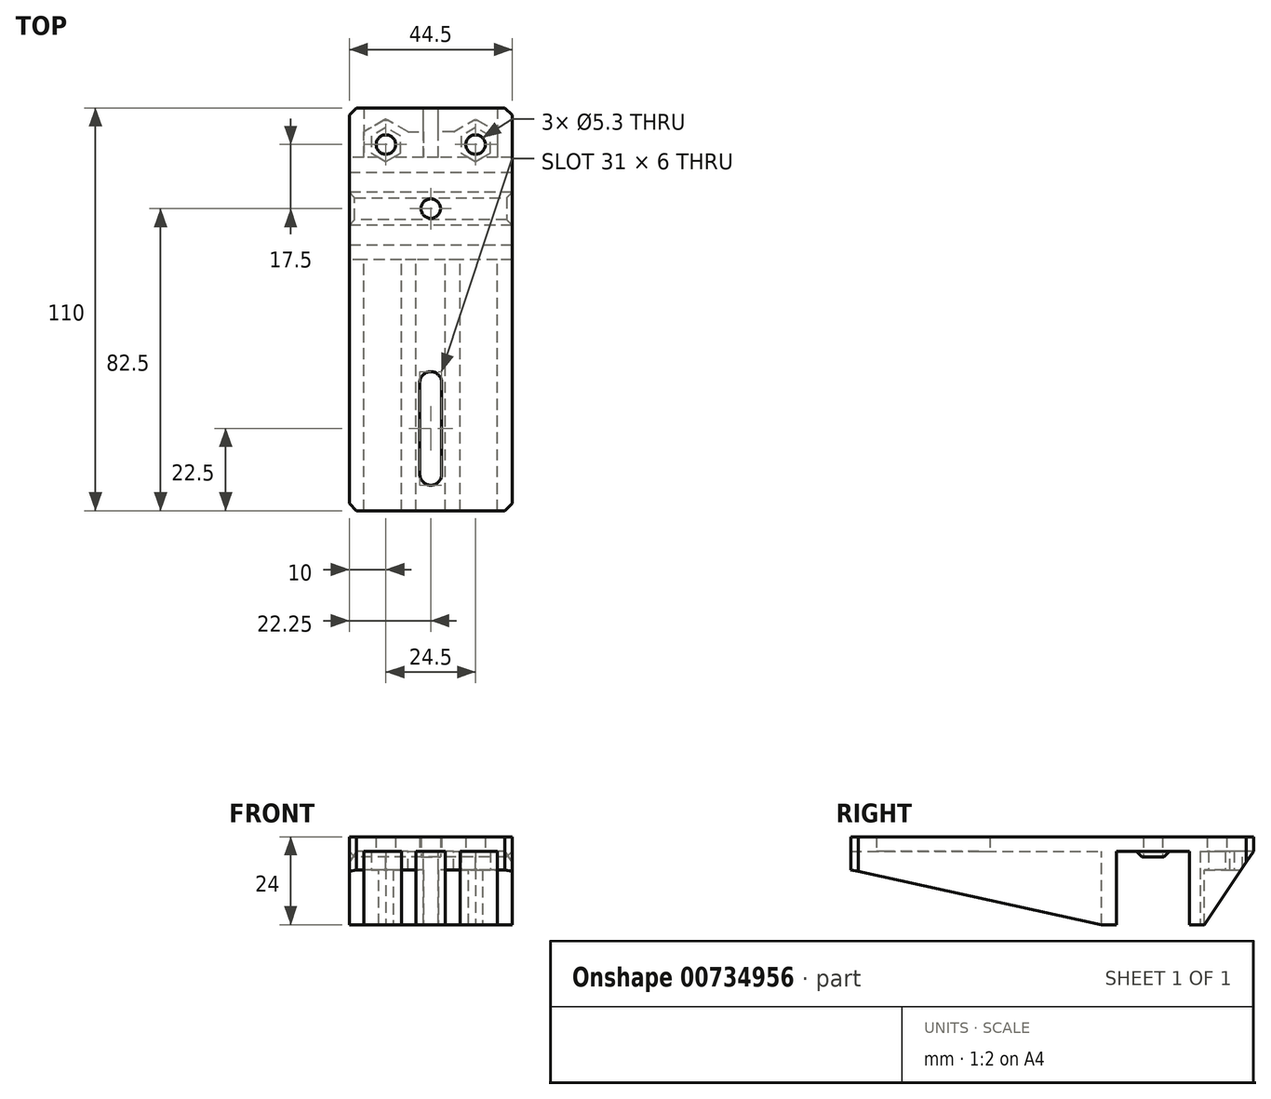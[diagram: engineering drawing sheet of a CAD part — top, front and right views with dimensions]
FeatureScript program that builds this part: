
annotation { "Feature Type Name" : "Feature", "Feature Type Description" : "" }
export const myFeature = defineFeature(function(context is Context, id is Id, definition is map)
    precondition{}
    {
        {
            var Q0;
            Q0=qCreatedBy(makeId("Top.planeOp"),FACE);
            var sketch = newSketch(context, id + "F0", { "sketchPlane" : qUnion([Q0])});
            skLineSegment(sketch, "E0.bottom", {"start": v(0, 0) * mm, "end": v(44.5, 0) * mm});
            skLineSegment(sketch, "E0.top", {"start": v(0, 110) * mm, "end": v(44.5, 110) * mm});
            skLineSegment(sketch, "E0.left", {"start": v(0, 0) * mm, "end": v(0, 110) * mm});
            skLineSegment(sketch, "E0.right", {"start": v(44.5, 0) * mm, "end": v(44.5, 110) * mm});
            skCircle(sketch, "E1", {"center": v(22.25, 10) * mm, "radius": 6.12 * mm, "construction": true});
            skPoint(sketch, "E1.centerSnap0", {"position": v(22.25, 0) * mm});
            skCircle(sketch, "E2", {"center": v(10, 100) * mm, "radius": 6.12 * mm, "construction": true});
            skCircle(sketch, "E3", {"center": v(34.5, 100) * mm, "radius": 6.12 * mm, "construction": true});
            skLineSegment(sketch, "E4", {"start": v(16.12, 100) * mm, "end": v(16.13, 10) * mm, "construction": true});
            skLineSegment(sketch, "E5", {"start": v(28.37, 10) * mm, "end": v(28.37, 100) * mm, "construction": true});
            skCircle(sketch, "E6", {"center": v(10, 100) * mm, "radius": 2.65 * mm});
            skCircle(sketch, "E7", {"center": v(34.5, 100) * mm, "radius": 2.65 * mm});
            skLineSegment(sketch, "E8", {"start": v(25.25, 10) * mm, "end": v(25.25, 35) * mm});
            skLineSegment(sketch, "E9", {"start": v(19.25, 35) * mm, "end": v(19.25, 10) * mm});
            skArc(sketch, "E10", {"start": v(19.25, 35) * mm, "mid": v(22.25, 32) * mm, "end": v(25.25, 35) * mm, "construction": true});
            skArc(sketch, "E11", {"start": v(25.25, 35) * mm, "mid": v(22.25, 38) * mm, "end": v(19.25, 35) * mm});
            skLineSegment(sketch, "E12", {"start": v(19.25, 10) * mm, "end": v(19.25, 10) * mm});
            skArc(sketch, "E13", {"start": v(25.25, 10) * mm, "mid": v(22.25, 13) * mm, "end": v(19.25, 10) * mm, "construction": true});
            skArc(sketch, "E14", {"start": v(19.25, 10) * mm, "mid": v(22.25, 7) * mm, "end": v(25.25, 10) * mm});
            skCircle(sketch, "E15", {"center": v(22.25, 82.5) * mm, "radius": 2.65 * mm});
            skSolve(sketch);
        }
        {
            var Q0;
            Q0 = qSketchRegion(id + "F0", true);
            extrude(context, id + "F1", {"entities" : qUnion([Q0]), "depth" : 4 * mm, "offsetDistance" : 25 * mm});
        }
        {
            var Q0;
            Q0=makeQuery(id+"F1.opExtrude","CAP_FACE",FACE,{"disambiguationData":[OSD([sQuery(id+"F0.wireOp",EDGE,"E0.bottom"),sQuery(id+"F0.wireOp",EDGE,"E0.top"),sQuery(id+"F0.wireOp",EDGE,"E0.left"),sQuery(id+"F0.wireOp",EDGE,"E0.right"),sQuery(id+"F0.wireOp",EDGE,"E6"),sQuery(id+"F0.wireOp",EDGE,"E7"),sQuery(id+"F0.wireOp",EDGE,"E8"),sQuery(id+"F0.wireOp",EDGE,"E9"),sQuery(id+"F0.wireOp",EDGE,"E11"),sQuery(id+"F0.wireOp",EDGE,"E14"),sQuery(id+"F0.wireOp",EDGE,"E15")])],"isStart":true});
            var sketch = newSketch(context, id + "F2", { "sketchPlane" : qUnion([Q0])});
            skLineSegment(sketch, "E16.bottom", {"start": v(0, -92.5) * mm, "end": v(44.5, -92.5) * mm});
            skLineSegment(sketch, "E16.top", {"start": v(0, -96.5) * mm, "end": v(44.5, -96.5) * mm});
            skLineSegment(sketch, "E16.left", {"start": v(0, -92.5) * mm, "end": v(0, -96.5) * mm});
            skLineSegment(sketch, "E16.right", {"start": v(44.5, -92.5) * mm, "end": v(44.5, -96.5) * mm});
            skLineSegment(sketch, "E17.bottom", {"start": v(44.5, -72.5) * mm, "end": v(0, -72.5) * mm});
            skLineSegment(sketch, "E17.top", {"start": v(44.5, -68.5) * mm, "end": v(0, -68.5) * mm});
            skLineSegment(sketch, "E17.left", {"start": v(44.5, -72.5) * mm, "end": v(44.5, -68.5) * mm});
            skLineSegment(sketch, "E17.right", {"start": v(0, -72.5) * mm, "end": v(0, -68.5) * mm});
            skCircle(sketch, "E18.0", {"center": v(22.25, -82.5) * mm, "radius": 2.65 * mm, "construction": true});
            skSolve(sketch);
        }
        {
            var Q0;
            Q0 = qSketchRegion(id + "F2", true);
            extrude(context, id + "F3", {"entities" : qUnion([Q0]), "operationType" : NewBodyOperationType.ADD, "depth" : 20 * mm, "offsetDistance" : 25 * mm});
        }
        {
            var Q0;
            {var subQ0=sQuery(id+"F0.wireOp",EDGE,"E9");var subQ1=sQuery(id+"F0.wireOp",EDGE,"E11");var subQ2=sQuery(id+"F0.wireOp",EDGE,"E14");var subQ3=sQuery(id+"F0.wireOp",EDGE,"E0.bottom");var subQ4=sQuery(id+"F0.wireOp",EDGE,"E8");var subQ5=sQuery(id+"F0.wireOp",EDGE,"E0.right");var subQ6=sQuery(id+"F0.wireOp",EDGE,"E0.left");Q0=makeQuery(id+"F3.boolean.opBoolean","SPLIT",FACE,{"disambiguationData":[TD([makeQuery(id+"F1.opExtrude","SWEPT_FACE",FACE,{"disambiguationData":[OSD([subQ3])]})])],"derivedFrom":makeQuery(id+"F1.opExtrude","CAP_FACE",FACE,{"disambiguationData":[OSD([subQ3,sQuery(id+"F0.wireOp",EDGE,"E0.top"),subQ6,subQ5,sQuery(id+"F0.wireOp",EDGE,"E6"),sQuery(id+"F0.wireOp",EDGE,"E7"),subQ4,subQ0,subQ1,subQ2,sQuery(id+"F0.wireOp",EDGE,"E15")])],"isStart":true})});}
            var sketch = newSketch(context, id + "F4", { "sketchPlane" : qUnion([Q0])});
            skLineSegment(sketch, "E19.bottom", {"start": v(0, 0) * mm, "end": v(4, 0) * mm});
            skLineSegment(sketch, "E19.top", {"start": v(0, -68.5) * mm, "end": v(4, -68.5) * mm});
            skLineSegment(sketch, "E19.left", {"start": v(0, 0) * mm, "end": v(0, -68.5) * mm});
            skLineSegment(sketch, "E19.right", {"start": v(4, 0) * mm, "end": v(4, -68.5) * mm});
            skLineSegment(sketch, "E20.bottom", {"start": v(44.5, 0) * mm, "end": v(40.5, 0) * mm});
            skLineSegment(sketch, "E20.top", {"start": v(44.5, -68.5) * mm, "end": v(40.5, -68.5) * mm});
            skLineSegment(sketch, "E20.left", {"start": v(44.5, 0) * mm, "end": v(44.5, -68.5) * mm});
            skLineSegment(sketch, "E20.right", {"start": v(40.5, 0) * mm, "end": v(40.5, -68.5) * mm});
            skLineSegment(sketch, "E21.0.0", {"start": v(44.5, -96.5) * mm, "end": v(0, -96.5) * mm, "construction": true});
            skLineSegment(sketch, "E21.0.1", {"start": v(0, -96.5) * mm, "end": v(0, -110) * mm, "construction": true});
            skLineSegment(sketch, "E21.0.3", {"start": v(44.5, -110) * mm, "end": v(44.5, -96.5) * mm, "construction": true});
            skLineSegment(sketch, "E22.bottom", {"start": v(0, -110) * mm, "end": v(4, -110) * mm});
            skLineSegment(sketch, "E22.top", {"start": v(0, -96.5) * mm, "end": v(4, -96.5) * mm});
            skLineSegment(sketch, "E22.left", {"start": v(0, -110) * mm, "end": v(0, -96.5) * mm});
            skLineSegment(sketch, "E22.right", {"start": v(4, -110) * mm, "end": v(4, -96.5) * mm});
            skLineSegment(sketch, "E23.bottom", {"start": v(44.5, -110) * mm, "end": v(40.5, -110) * mm});
            skLineSegment(sketch, "E23.top", {"start": v(44.5, -96.5) * mm, "end": v(40.5, -96.5) * mm});
            skLineSegment(sketch, "E23.left", {"start": v(44.5, -110) * mm, "end": v(44.5, -96.5) * mm});
            skLineSegment(sketch, "E23.right", {"start": v(40.5, -110) * mm, "end": v(40.5, -96.5) * mm});
            skLineSegment(sketch, "E24.bottom", {"start": v(14.25, 0) * mm, "end": v(18.25, 0) * mm});
            skLineSegment(sketch, "E24.top", {"start": v(14.25, -68.5) * mm, "end": v(18.25, -68.5) * mm});
            skLineSegment(sketch, "E24.left", {"start": v(14.25, 0) * mm, "end": v(14.25, -68.5) * mm});
            skLineSegment(sketch, "E24.right", {"start": v(18.25, 0) * mm, "end": v(18.25, -68.5) * mm});
            skLineSegment(sketch, "E25.bottom", {"start": v(30.25, 0) * mm, "end": v(26.25, 0) * mm});
            skLineSegment(sketch, "E25.top", {"start": v(30.25, -68.5) * mm, "end": v(26.25, -68.5) * mm});
            skLineSegment(sketch, "E25.left", {"start": v(30.25, 0) * mm, "end": v(30.25, -68.5) * mm});
            skLineSegment(sketch, "E25.right", {"start": v(26.25, 0) * mm, "end": v(26.25, -68.5) * mm});
            skLineSegment(sketch, "E26.bottom", {"start": v(24.25, -96.5) * mm, "end": v(20.25, -96.5) * mm});
            skLineSegment(sketch, "E26.top", {"start": v(24.25, -110) * mm, "end": v(20.25, -110) * mm});
            skLineSegment(sketch, "E26.left", {"start": v(24.25, -96.5) * mm, "end": v(24.25, -110) * mm});
            skLineSegment(sketch, "E26.right", {"start": v(20.25, -96.5) * mm, "end": v(20.25, -110) * mm});
            skPoint(sketch, "E26.middle", {"position": v(22.25, -103.25) * mm});
            skPoint(sketch, "E26.middle.positionSnap0", {"position": v(40.5, -103.25) * mm});
            skPoint(sketch, "E26.middle.positionSnap1", {"position": v(22.25, -96.5) * mm});
            skPoint(sketch, "E26.centerSnap0", {"position": v(40.5, -103.25) * mm});
            skPoint(sketch, "E26.centerSnap1", {"position": v(22.25, -96.5) * mm});
            skCircle(sketch, "E27.0", {"center": v(10, -100) * mm, "radius": 2.65 * mm, "construction": true});
            skCircle(sketch, "E28.0", {"center": v(34.5, -100) * mm, "radius": 2.65 * mm, "construction": true});
            skCircle(sketch, "E29.cCircle", {"center": v(10, -100) * mm, "radius": 4 * mm, "construction": true});
            skLineSegment(sketch, "E29.0", {"start": v(6, -102.3) * mm, "end": v(6, -97.7) * mm});
            skLineSegment(sketch, "E29.1", {"start": v(6, -97.7) * mm, "end": v(8.06, -96.5) * mm});
            skLineSegment(sketch, "E29.2", {"start": v(10, -95.38) * mm, "end": v(11.94, -96.5) * mm, "construction": true});
            skLineSegment(sketch, "E29.3", {"start": v(14, -97.7) * mm, "end": v(14, -102.3) * mm});
            skLineSegment(sketch, "E29.4", {"start": v(14, -102.3) * mm, "end": v(10, -104.62) * mm});
            skLineSegment(sketch, "E29.5", {"start": v(10, -104.62) * mm, "end": v(6, -102.3) * mm});
            skPoint(sketch, "E29.0.midPoint", {"position": v(6, -100) * mm});
            skCircle(sketch, "E30.cCircle", {"center": v(10, -100) * mm, "radius": 6 * mm, "construction": true});
            skLineSegment(sketch, "E30.0", {"start": v(16, -96.54) * mm, "end": v(16, -103.46) * mm});
            skLineSegment(sketch, "E30.1", {"start": v(16, -103.46) * mm, "end": v(10, -106.93) * mm});
            skLineSegment(sketch, "E30.2", {"start": v(10, -106.93) * mm, "end": v(4, -103.46) * mm});
            skLineSegment(sketch, "E30.3", {"start": v(4, -103.46) * mm, "end": v(4, -96.54) * mm, "construction": true});
            skLineSegment(sketch, "E30.4", {"start": v(4, -96.54) * mm, "end": v(4.06, -96.5) * mm});
            skLineSegment(sketch, "E30.5", {"start": v(10, -93.07) * mm, "end": v(15.94, -96.5) * mm, "construction": true});
            skPoint(sketch, "E30.0.midPoint", {"position": v(16, -100) * mm});
            skLineSegment(sketch, "E31", {"start": v(4.06, -96.5) * mm, "end": v(10, -93.07) * mm, "construction": true});
            skLineSegment(sketch, "E32", {"start": v(15.94, -96.5) * mm, "end": v(16, -96.54) * mm});
            skLineSegment(sketch, "E33", {"start": v(4.06, -96.5) * mm, "end": v(15.94, -96.5) * mm});
            skLineSegment(sketch, "E34", {"start": v(22.25, -103.25) * mm, "end": v(22.25, -96.5) * mm, "construction": true});
            skLineSegment(sketch, "E35.MirrorCS", {"start": v(34.5, -93.07) * mm, "end": v(28.56, -96.5) * mm, "construction": true});
            skLineSegment(sketch, "E36.MirrorCS", {"start": v(40.44, -96.5) * mm, "end": v(28.56, -96.5) * mm});
            skLineSegment(sketch, "E37.MirrorCS", {"start": v(40.44, -96.5) * mm, "end": v(34.5, -93.07) * mm, "construction": true});
            skPoint(sketch, "E38.MirrorP", {"position": v(38.5, -100) * mm});
            skLineSegment(sketch, "E39.MirrorCS", {"start": v(28.5, -96.54) * mm, "end": v(28.5, -103.46) * mm});
            skCircle(sketch, "E40.MirrorC", {"center": v(34.5, -100) * mm, "radius": 4 * mm, "construction": true});
            skLineSegment(sketch, "E41.MirrorCS", {"start": v(30.5, -97.7) * mm, "end": v(30.5, -102.3) * mm});
            skCircle(sketch, "E42.MirrorC", {"center": v(34.5, -100) * mm, "radius": 6 * mm, "construction": true});
            skLineSegment(sketch, "E43.MirrorCS", {"start": v(40.5, -103.46) * mm, "end": v(40.5, -96.54) * mm, "construction": true});
            skPoint(sketch, "E44.MirrorP", {"position": v(28.5, -100) * mm});
            skLineSegment(sketch, "E45.MirrorCS", {"start": v(34.5, -104.62) * mm, "end": v(38.5, -102.3) * mm});
            skLineSegment(sketch, "E46.MirrorCS", {"start": v(34.5, -106.93) * mm, "end": v(40.5, -103.46) * mm});
            skLineSegment(sketch, "E47.MirrorCS", {"start": v(28.56, -96.5) * mm, "end": v(28.5, -96.54) * mm});
            skLineSegment(sketch, "E48.MirrorCS", {"start": v(28.5, -103.46) * mm, "end": v(34.5, -106.93) * mm});
            skLineSegment(sketch, "E49.MirrorCS", {"start": v(40.5, -96.54) * mm, "end": v(40.44, -96.5) * mm});
            skLineSegment(sketch, "E50.MirrorCS", {"start": v(34.5, -95.38) * mm, "end": v(30.5, -97.7) * mm});
            skLineSegment(sketch, "E51.MirrorCS", {"start": v(38.5, -102.3) * mm, "end": v(38.5, -97.7) * mm});
            skLineSegment(sketch, "E52.MirrorCS", {"start": v(30.5, -102.3) * mm, "end": v(34.5, -104.62) * mm});
            skLineSegment(sketch, "E53.MirrorCS", {"start": v(38.5, -97.7) * mm, "end": v(34.5, -95.38) * mm});
            skLineSegment(sketch, "E54", {"start": v(32.56, -96.5) * mm, "end": v(36.44, -96.5) * mm});
            skLineSegment(sketch, "E55", {"start": v(11.94, -96.5) * mm, "end": v(14, -97.7) * mm});
            skLineSegment(sketch, "E56", {"start": v(8.06, -96.5) * mm, "end": v(10, -95.38) * mm, "construction": true});
            skLineSegment(sketch, "E57", {"start": v(8.06, -96.5) * mm, "end": v(11.94, -96.5) * mm});
            skSolve(sketch);
        }
        {
            var Q0;
            Q0 = qSketchRegion(id + "F4", true);
            extrude(context, id + "F5", {"entities" : qUnion([Q0]), "operationType" : NewBodyOperationType.ADD, "depth" : 20 * mm, "offsetDistance" : 25 * mm});
        }
        {
            var Q0;
            {var subQ1=sQuery(id+"F0.wireOp",EDGE,"E0.top");var subQ2=makeQuery(id+"F1.opExtrude","SWEPT_FACE",FACE,{"disambiguationData":[OSD([subQ1])]});var subQ6=sQuery(id+"F0.wireOp",EDGE,"E6");var subQ7=sQuery(id+"F0.wireOp",EDGE,"E0.right");var subQ8=sQuery(id+"F0.wireOp",EDGE,"E0.left");var subQ9=sQuery(id+"F0.wireOp",EDGE,"E7");Q0=makeQuery(id+"F5.boolean.opBoolean","SPLIT",FACE,{"disambiguationData":[TD([makeQuery(id+"F5.opExtrude","SWEPT_FACE",FACE,{"disambiguationData":[OSD([sQuery(id+"F4.wireOp",EDGE,"E26.right")])]})])],"derivedFrom":makeQuery(id+"F3.boolean.opBoolean","SPLIT",FACE,{"disambiguationData":[TD([subQ2])],"derivedFrom":makeQuery(id+"F1.opExtrude","CAP_FACE",FACE,{"disambiguationData":[OSD([sQuery(id+"F0.wireOp",EDGE,"E0.bottom"),subQ1,subQ8,subQ7,subQ6,subQ9,sQuery(id+"F0.wireOp",EDGE,"E8"),sQuery(id+"F0.wireOp",EDGE,"E9"),sQuery(id+"F0.wireOp",EDGE,"E11"),sQuery(id+"F0.wireOp",EDGE,"E14"),sQuery(id+"F0.wireOp",EDGE,"E15")])],"isStart":true})})});}
            var sketch = newSketch(context, id + "F6", { "sketchPlane" : qUnion([Q0])});
            skLineSegment(sketch, "E58.0.0", {"start": v(40.44, -96.5) * mm, "end": v(40.5, -96.54) * mm});
            skLineSegment(sketch, "E58.0.1", {"start": v(40.5, -96.54) * mm, "end": v(40.5, -96.5) * mm});
            skLineSegment(sketch, "E58.0.2", {"start": v(40.5, -96.5) * mm, "end": v(40.44, -96.5) * mm});
            skLineSegment(sketch, "E59.0.0", {"start": v(4, -96.5) * mm, "end": v(4, -96.54) * mm});
            skLineSegment(sketch, "E59.0.1", {"start": v(4, -96.54) * mm, "end": v(4.06, -96.5) * mm});
            skLineSegment(sketch, "E59.0.2", {"start": v(4.06, -96.5) * mm, "end": v(4, -96.5) * mm});
            skLineSegment(sketch, "E60", {"start": v(16, -103.46) * mm, "end": v(20.25, -103.46) * mm});
            skLineSegment(sketch, "E61", {"start": v(20.25, -103.46) * mm, "end": v(20.25, -96.5) * mm});
            skLineSegment(sketch, "E62", {"start": v(20.25, -96.5) * mm, "end": v(20.25, -103.46) * mm});
            skLineSegment(sketch, "E63.0", {"start": v(24.25, -96.5) * mm, "end": v(28.56, -96.5) * mm});
            skLineSegment(sketch, "E64.0", {"start": v(15.94, -96.5) * mm, "end": v(20.25, -96.5) * mm});
            skPoint(sketch, "E65.0", {"position": v(15.97, -96.52) * mm});
            skLineSegment(sketch, "E66.0", {"start": v(15.94, -96.5) * mm, "end": v(16, -96.54) * mm});
            skLineSegment(sketch, "E67.0", {"start": v(16, -96.54) * mm, "end": v(16, -103.46) * mm});
            skLineSegment(sketch, "E68.0", {"start": v(28.5, -96.54) * mm, "end": v(28.5, -103.46) * mm});
            skLineSegment(sketch, "E69.0", {"start": v(28.56, -96.5) * mm, "end": v(28.5, -96.54) * mm});
            skLineSegment(sketch, "E70", {"start": v(28.5, -103.46) * mm, "end": v(24.25, -103.46) * mm});
            skLineSegment(sketch, "E71", {"start": v(24.25, -103.46) * mm, "end": v(24.25, -96.5) * mm});
            skSolve(sketch);
        }
        {
            var Q0;
            Q0 = qSketchRegion(id + "F6", true);
            extrude(context, id + "F7", {"entities" : qUnion([Q0]), "operationType" : NewBodyOperationType.ADD, "depth" : 20 * mm, "offsetDistance" : 25 * mm});
        }
        {
            var Q0;
            Q0=makeQuery(id+"F7.boolean.opBoolean","MERGE",FACE,{"derivedFrom":[makeQuery(id+"F5.boolean.opBoolean","MERGE",FACE,{"derivedFrom":[makeQuery(id+"F3.opExtrude","CAP_FACE",FACE,{"disambiguationData":[OSD([sQuery(id+"F2.wireOp",EDGE,"E16.bottom"),sQuery(id+"F2.wireOp",EDGE,"E16.top"),sQuery(id+"F2.wireOp",EDGE,"E16.left"),sQuery(id+"F2.wireOp",EDGE,"E16.right")])],"isStart":false}),makeQuery(id+"F5.opExtrude","CAP_FACE",FACE,{"disambiguationData":[OSD([sQuery(id+"F4.wireOp",EDGE,"E22.bottom"),sQuery(id+"F4.wireOp",EDGE,"E22.top"),sQuery(id+"F4.wireOp",EDGE,"E22.left"),sQuery(id+"F4.wireOp",EDGE,"E22.right"),sQuery(id+"F4.wireOp",EDGE,"E29.0"),sQuery(id+"F4.wireOp",EDGE,"E29.1"),sQuery(id+"F4.wireOp",EDGE,"E29.2"),sQuery(id+"F4.wireOp",EDGE,"E29.3"),sQuery(id+"F4.wireOp",EDGE,"E29.4"),sQuery(id+"F4.wireOp",EDGE,"E29.5"),sQuery(id+"F4.wireOp",EDGE,"E30.0"),sQuery(id+"F4.wireOp",EDGE,"E30.1"),sQuery(id+"F4.wireOp",EDGE,"E30.2"),sQuery(id+"F4.wireOp",EDGE,"E30.4"),sQuery(id+"F4.wireOp",EDGE,"E32"),sQuery(id+"F4.wireOp",EDGE,"E33")])],"isStart":false}),makeQuery(id+"F5.opExtrude","CAP_FACE",FACE,{"disambiguationData":[OSD([sQuery(id+"F4.wireOp",EDGE,"E23.bottom"),sQuery(id+"F4.wireOp",EDGE,"E23.top"),sQuery(id+"F4.wireOp",EDGE,"E23.left"),sQuery(id+"F4.wireOp",EDGE,"E23.right"),sQuery(id+"F4.wireOp",EDGE,"E36.MirrorCS"),sQuery(id+"F4.wireOp",EDGE,"E39.MirrorCS"),sQuery(id+"F4.wireOp",EDGE,"E41.MirrorCS"),sQuery(id+"F4.wireOp",EDGE,"E45.MirrorCS"),sQuery(id+"F4.wireOp",EDGE,"E46.MirrorCS"),sQuery(id+"F4.wireOp",EDGE,"E47.MirrorCS"),sQuery(id+"F4.wireOp",EDGE,"E48.MirrorCS"),sQuery(id+"F4.wireOp",EDGE,"E49.MirrorCS"),sQuery(id+"F4.wireOp",EDGE,"E50.MirrorCS"),sQuery(id+"F4.wireOp",EDGE,"E51.MirrorCS"),sQuery(id+"F4.wireOp",EDGE,"E52.MirrorCS"),sQuery(id+"F4.wireOp",EDGE,"E53.MirrorCS")])],"isStart":false}),makeQuery(id+"F5.opExtrude","CAP_FACE",FACE,{"disambiguationData":[OSD([sQuery(id+"F4.wireOp",EDGE,"E26.bottom"),sQuery(id+"F4.wireOp",EDGE,"E26.top"),sQuery(id+"F4.wireOp",EDGE,"E26.left"),sQuery(id+"F4.wireOp",EDGE,"E26.right")])],"isStart":false})]}),makeQuery(id+"F7.opExtrude","CAP_FACE",FACE,{"disambiguationData":[OSD([sQuery(id+"F6.wireOp",EDGE,"E58.0.0"),sQuery(id+"F6.wireOp",EDGE,"E58.0.1"),sQuery(id+"F6.wireOp",EDGE,"E58.0.2")])],"isStart":false}),makeQuery(id+"F7.opExtrude","CAP_FACE",FACE,{"disambiguationData":[OSD([sQuery(id+"F6.wireOp",EDGE,"E59.0.0"),sQuery(id+"F6.wireOp",EDGE,"E59.0.1"),sQuery(id+"F6.wireOp",EDGE,"E59.0.2")])],"isStart":false}),makeQuery(id+"F7.opExtrude","CAP_FACE",FACE,{"disambiguationData":[OSD([sQuery(id+"F6.wireOp",EDGE,"E60"),sQuery(id+"F6.wireOp",EDGE,"E62"),sQuery(id+"F6.wireOp",EDGE,"E64.0"),sQuery(id+"F6.wireOp",EDGE,"E66.0"),sQuery(id+"F6.wireOp",EDGE,"E67.0")])],"isStart":false}),makeQuery(id+"F7.opExtrude","CAP_FACE",FACE,{"disambiguationData":[OSD([sQuery(id+"F6.wireOp",EDGE,"E63.0"),sQuery(id+"F6.wireOp",EDGE,"E68.0"),sQuery(id+"F6.wireOp",EDGE,"E69.0"),sQuery(id+"F6.wireOp",EDGE,"E70"),sQuery(id+"F6.wireOp",EDGE,"E71")])],"isStart":false})]});
            var sketch = newSketch(context, id + "F8", { "sketchPlane" : qUnion([Q0])});
            skLineSegment(sketch, "E72.0", {"start": v(10, -106.93) * mm, "end": v(4, -103.46) * mm});
            skLineSegment(sketch, "E73.0", {"start": v(16, -103.46) * mm, "end": v(10, -106.93) * mm});
            skLineSegment(sketch, "E74.0", {"start": v(16, -103.46) * mm, "end": v(20.25, -103.46) * mm});
            skLineSegment(sketch, "E75.0", {"start": v(28.5, -103.46) * mm, "end": v(24.25, -103.46) * mm});
            skLineSegment(sketch, "E76.0", {"start": v(28.5, -103.46) * mm, "end": v(34.5, -106.93) * mm});
            skPoint(sketch, "E77.0", {"position": v(37.5, -105.2) * mm});
            skLineSegment(sketch, "E78.0", {"start": v(34.5, -106.93) * mm, "end": v(40.5, -103.46) * mm});
            skLineSegment(sketch, "E79", {"start": v(40.5, -103.46) * mm, "end": v(40.5, -96.5) * mm});
            skLineSegment(sketch, "E80", {"start": v(40.5, -96.5) * mm, "end": v(24.25, -96.5) * mm});
            skLineSegment(sketch, "E81", {"start": v(24.25, -96.5) * mm, "end": v(24.25, -103.46) * mm});
            skLineSegment(sketch, "E82", {"start": v(20.25, -103.46) * mm, "end": v(20.25, -96.5) * mm});
            skLineSegment(sketch, "E83", {"start": v(20.25, -96.5) * mm, "end": v(4, -96.5) * mm});
            skLineSegment(sketch, "E84", {"start": v(4, -96.5) * mm, "end": v(4, -103.46) * mm});
            skSolve(sketch);
        }
        {
            var Q0;
            Q0 = qSketchRegion(id + "F8", true);
            extrude(context, id + "F9", {"entities" : qUnion([Q0]), "operationType" : NewBodyOperationType.REMOVE, "oppositeDirection" : true, "depth" : 15 * mm, "offsetDistance" : 25 * mm});
        }
        {
            var Q0;
            Q0=makeQuery(id+"F5.boolean.opBoolean","MERGE",FACE,{"derivedFrom":[makeQuery(id+"F3.boolean.opBoolean","MERGE",FACE,{"derivedFrom":[makeQuery(id+"F1.opExtrude","SWEPT_FACE",FACE,{"disambiguationData":[OSD([sQuery(id+"F0.wireOp",EDGE,"E0.left")])]}),makeQuery(id+"F3.opExtrude","SWEPT_FACE",FACE,{"disambiguationData":[OSD([sQuery(id+"F2.wireOp",EDGE,"E16.left")])]}),makeQuery(id+"F3.opExtrude","SWEPT_FACE",FACE,{"disambiguationData":[OSD([sQuery(id+"F2.wireOp",EDGE,"E17.right")])]})]}),makeQuery(id+"F5.opExtrude","SWEPT_FACE",FACE,{"disambiguationData":[OSD([sQuery(id+"F4.wireOp",EDGE,"E19.left")])]}),makeQuery(id+"F5.opExtrude","SWEPT_FACE",FACE,{"disambiguationData":[OSD([sQuery(id+"F4.wireOp",EDGE,"E22.left")])]})]});
            var sketch = newSketch(context, id + "F10", { "sketchPlane" : qUnion([Q0])});
            skLineSegment(sketch, "E85", {"start": v(-110, 0) * mm, "end": v(-96.5, -20) * mm});
            skLineSegment(sketch, "E86", {"start": v(-96.5, -20) * mm, "end": v(-110, -20) * mm});
            skLineSegment(sketch, "E87", {"start": v(-110, -20) * mm, "end": v(-110, 0) * mm});
            skLineSegment(sketch, "E88", {"start": v(-68.5, -20) * mm, "end": v(0, -5) * mm});
            skLineSegment(sketch, "E89", {"start": v(0, -5) * mm, "end": v(0, -20) * mm});
            skLineSegment(sketch, "E90", {"start": v(0, -20) * mm, "end": v(-68.5, -20) * mm});
            skSolve(sketch);
        }
        {
            var Q0;
            Q0 = qSketchRegion(id + "F10", true);
            extrude(context, id + "F11", {"entities" : qUnion([Q0]), "operationType" : NewBodyOperationType.REMOVE, "endBound" : BoundingType.THROUGH_ALL, "oppositeDirection" : true, "depth" : 25 * mm, "offsetDistance" : 25 * mm});
        }
        {
            var Q0;
            Q0=makeQuery(id+"F5.opExtrude","CAP_FACE",FACE,{"disambiguationData":[OSD([sQuery(id+"F4.wireOp",EDGE,"E23.bottom"),sQuery(id+"F4.wireOp",EDGE,"E23.top"),sQuery(id+"F4.wireOp",EDGE,"E23.left"),sQuery(id+"F4.wireOp",EDGE,"E23.right"),sQuery(id+"F4.wireOp",EDGE,"E36.MirrorCS"),sQuery(id+"F4.wireOp",EDGE,"E39.MirrorCS"),sQuery(id+"F4.wireOp",EDGE,"E46.MirrorCS"),sQuery(id+"F4.wireOp",EDGE,"E47.MirrorCS"),sQuery(id+"F4.wireOp",EDGE,"E48.MirrorCS"),sQuery(id+"F4.wireOp",EDGE,"E49.MirrorCS"),sQuery(id+"F4.wireOp",EDGE,"E50.MirrorCS"),sQuery(id+"F4.wireOp",EDGE,"E53.MirrorCS")])],"isStart":true});
            var Q1;
            Q1=makeQuery(id+"F5.opExtrude","CAP_FACE",FACE,{"disambiguationData":[OSD([sQuery(id+"F4.wireOp",EDGE,"E22.bottom"),sQuery(id+"F4.wireOp",EDGE,"E22.top"),sQuery(id+"F4.wireOp",EDGE,"E22.left"),sQuery(id+"F4.wireOp",EDGE,"E22.right"),sQuery(id+"F4.wireOp",EDGE,"E30.0"),sQuery(id+"F4.wireOp",EDGE,"E30.1"),sQuery(id+"F4.wireOp",EDGE,"E30.2"),sQuery(id+"F4.wireOp",EDGE,"E30.4"),sQuery(id+"F4.wireOp",EDGE,"E32"),sQuery(id+"F4.wireOp",EDGE,"E33"),sQuery(id+"F4.wireOp",EDGE,"E57")])],"isStart":true});
            extrude(context, id + "F12", {"entities" : qUnion([Q0, Q1]), "operationType" : NewBodyOperationType.REMOVE, "endBound" : BoundingType.THROUGH_ALL, "oppositeDirection" : true, "depth" : 25 * mm, "offsetDistance" : 25 * mm});
        }
        {
            var Q0;
            Q0=makeQuery(id+"F7.boolean.opBoolean","MERGE",FACE,{"derivedFrom":[makeQuery(id+"F5.boolean.opBoolean","MERGE",FACE,{"derivedFrom":[makeQuery(id+"F3.opExtrude","CAP_FACE",FACE,{"disambiguationData":[OSD([sQuery(id+"F2.wireOp",EDGE,"E16.bottom"),sQuery(id+"F2.wireOp",EDGE,"E16.top"),sQuery(id+"F2.wireOp",EDGE,"E16.left"),sQuery(id+"F2.wireOp",EDGE,"E16.right")])],"isStart":false}),makeQuery(id+"F5.opExtrude","CAP_FACE",FACE,{"disambiguationData":[OSD([sQuery(id+"F4.wireOp",EDGE,"E22.bottom"),sQuery(id+"F4.wireOp",EDGE,"E22.top"),sQuery(id+"F4.wireOp",EDGE,"E22.left"),sQuery(id+"F4.wireOp",EDGE,"E22.right"),sQuery(id+"F4.wireOp",EDGE,"E30.0"),sQuery(id+"F4.wireOp",EDGE,"E30.1"),sQuery(id+"F4.wireOp",EDGE,"E30.2"),sQuery(id+"F4.wireOp",EDGE,"E30.4"),sQuery(id+"F4.wireOp",EDGE,"E32"),sQuery(id+"F4.wireOp",EDGE,"E33"),sQuery(id+"F4.wireOp",EDGE,"E57")])],"isStart":false}),makeQuery(id+"F5.opExtrude","CAP_FACE",FACE,{"disambiguationData":[OSD([sQuery(id+"F4.wireOp",EDGE,"E23.bottom"),sQuery(id+"F4.wireOp",EDGE,"E23.top"),sQuery(id+"F4.wireOp",EDGE,"E23.left"),sQuery(id+"F4.wireOp",EDGE,"E23.right"),sQuery(id+"F4.wireOp",EDGE,"E36.MirrorCS"),sQuery(id+"F4.wireOp",EDGE,"E39.MirrorCS"),sQuery(id+"F4.wireOp",EDGE,"E46.MirrorCS"),sQuery(id+"F4.wireOp",EDGE,"E47.MirrorCS"),sQuery(id+"F4.wireOp",EDGE,"E48.MirrorCS"),sQuery(id+"F4.wireOp",EDGE,"E49.MirrorCS"),sQuery(id+"F4.wireOp",EDGE,"E50.MirrorCS"),sQuery(id+"F4.wireOp",EDGE,"E53.MirrorCS")])],"isStart":false}),makeQuery(id+"F5.opExtrude","CAP_FACE",FACE,{"disambiguationData":[OSD([sQuery(id+"F4.wireOp",EDGE,"E26.bottom"),sQuery(id+"F4.wireOp",EDGE,"E26.top"),sQuery(id+"F4.wireOp",EDGE,"E26.left"),sQuery(id+"F4.wireOp",EDGE,"E26.right")])],"isStart":false})]}),makeQuery(id+"F7.opExtrude","CAP_FACE",FACE,{"disambiguationData":[OSD([sQuery(id+"F6.wireOp",EDGE,"E58.0.0"),sQuery(id+"F6.wireOp",EDGE,"E58.0.1"),sQuery(id+"F6.wireOp",EDGE,"E58.0.2")])],"isStart":false}),makeQuery(id+"F7.opExtrude","CAP_FACE",FACE,{"disambiguationData":[OSD([sQuery(id+"F6.wireOp",EDGE,"E59.0.0"),sQuery(id+"F6.wireOp",EDGE,"E59.0.1"),sQuery(id+"F6.wireOp",EDGE,"E59.0.2")])],"isStart":false}),makeQuery(id+"F7.opExtrude","CAP_FACE",FACE,{"disambiguationData":[OSD([sQuery(id+"F6.wireOp",EDGE,"E60"),sQuery(id+"F6.wireOp",EDGE,"E62"),sQuery(id+"F6.wireOp",EDGE,"E64.0"),sQuery(id+"F6.wireOp",EDGE,"E66.0"),sQuery(id+"F6.wireOp",EDGE,"E67.0")])],"isStart":false}),makeQuery(id+"F7.opExtrude","CAP_FACE",FACE,{"disambiguationData":[OSD([sQuery(id+"F6.wireOp",EDGE,"E63.0"),sQuery(id+"F6.wireOp",EDGE,"E68.0"),sQuery(id+"F6.wireOp",EDGE,"E69.0"),sQuery(id+"F6.wireOp",EDGE,"E70"),sQuery(id+"F6.wireOp",EDGE,"E71")])],"isStart":false})]});
            var sketch = newSketch(context, id + "F13", { "sketchPlane" : qUnion([Q0])});
            skCircle(sketch, "E91.0", {"center": v(10, -100) * mm, "radius": 2.65 * mm, "construction": true});
            skCircle(sketch, "E92.0", {"center": v(34.5, -100) * mm, "radius": 2.65 * mm, "construction": true});
            skCircle(sketch, "E93.cCircle", {"center": v(10, -100) * mm, "radius": 4 * mm, "construction": true});
            skLineSegment(sketch, "E93.0", {"start": v(14, -97.7) * mm, "end": v(14, -102.3) * mm});
            skLineSegment(sketch, "E93.1", {"start": v(14, -102.3) * mm, "end": v(10, -104.62) * mm});
            skLineSegment(sketch, "E93.2", {"start": v(10, -104.62) * mm, "end": v(6, -102.3) * mm});
            skLineSegment(sketch, "E93.3", {"start": v(6, -102.3) * mm, "end": v(6, -97.7) * mm});
            skLineSegment(sketch, "E93.4", {"start": v(6, -97.7) * mm, "end": v(10, -95.38) * mm});
            skLineSegment(sketch, "E93.5", {"start": v(10, -95.38) * mm, "end": v(14, -97.7) * mm});
            skPoint(sketch, "E93.0.midPoint", {"position": v(14, -100) * mm});
            skCircle(sketch, "E94.cCircle", {"center": v(34.5, -100) * mm, "radius": 4 * mm, "construction": true});
            skLineSegment(sketch, "E94.0", {"start": v(38.5, -97.7) * mm, "end": v(38.5, -102.3) * mm});
            skLineSegment(sketch, "E94.1", {"start": v(38.5, -102.3) * mm, "end": v(34.5, -104.62) * mm});
            skLineSegment(sketch, "E94.2", {"start": v(34.5, -104.62) * mm, "end": v(30.5, -102.3) * mm});
            skLineSegment(sketch, "E94.3", {"start": v(30.5, -102.3) * mm, "end": v(30.5, -97.7) * mm});
            skLineSegment(sketch, "E94.4", {"start": v(30.5, -97.7) * mm, "end": v(34.5, -95.38) * mm});
            skLineSegment(sketch, "E94.5", {"start": v(34.5, -95.38) * mm, "end": v(38.5, -97.7) * mm});
            skPoint(sketch, "E94.0.midPoint", {"position": v(38.5, -100) * mm});
            skSolve(sketch);
        }
        {
            var Q0;
            Q0 = qSketchRegion(id + "F13", true);
            var Q1;
            {var subQ1=sQuery(id+"F0.wireOp",EDGE,"E0.top");var subQ2=makeQuery(id+"F1.opExtrude","SWEPT_FACE",FACE,{"disambiguationData":[OSD([subQ1])]});var subQ6=sQuery(id+"F0.wireOp",EDGE,"E6");var subQ7=sQuery(id+"F0.wireOp",EDGE,"E0.right");var subQ8=sQuery(id+"F0.wireOp",EDGE,"E0.left");var subQ9=sQuery(id+"F0.wireOp",EDGE,"E7");Q1=makeQuery(id+"F5.boolean.opBoolean","SPLIT",FACE,{"disambiguationData":[TD([makeQuery(id+"F5.opExtrude","SWEPT_FACE",FACE,{"disambiguationData":[OSD([sQuery(id+"F4.wireOp",EDGE,"E26.right")])]})])],"derivedFrom":makeQuery(id+"F3.boolean.opBoolean","SPLIT",FACE,{"disambiguationData":[TD([subQ2])],"derivedFrom":makeQuery(id+"F1.opExtrude","CAP_FACE",FACE,{"disambiguationData":[OSD([sQuery(id+"F0.wireOp",EDGE,"E0.bottom"),subQ1,subQ8,subQ7,subQ6,subQ9,sQuery(id+"F0.wireOp",EDGE,"E8"),sQuery(id+"F0.wireOp",EDGE,"E9"),sQuery(id+"F0.wireOp",EDGE,"E11"),sQuery(id+"F0.wireOp",EDGE,"E14"),sQuery(id+"F0.wireOp",EDGE,"E15")])],"isStart":true})})});}
            extrude(context, id + "F14", {"entities" : qUnion([Q0]), "operationType" : NewBodyOperationType.REMOVE, "endBound" : BoundingType.UP_TO_SURFACE, "oppositeDirection" : true, "depth" : 25 * mm, "endBoundEntityFace" : qUnion([Q1]), "offsetDistance" : 25 * mm});
        }
        {
            var Q0;
            {var subQ0=sQuery(id+"F0.wireOp",EDGE,"E15");var subQ1=sQuery(id+"F0.wireOp",EDGE,"E0.right");var subQ2=sQuery(id+"F0.wireOp",EDGE,"E0.left");Q0=makeQuery(id+"F3.boolean.opBoolean","SPLIT",FACE,{"disambiguationData":[TD([makeQuery(id+"F1.opExtrude","SWEPT_FACE",FACE,{"disambiguationData":[OSD([subQ0])]})])],"derivedFrom":makeQuery(id+"F1.opExtrude","CAP_FACE",FACE,{"disambiguationData":[OSD([sQuery(id+"F0.wireOp",EDGE,"E0.bottom"),sQuery(id+"F0.wireOp",EDGE,"E0.top"),subQ2,subQ1,sQuery(id+"F0.wireOp",EDGE,"E6"),sQuery(id+"F0.wireOp",EDGE,"E7"),sQuery(id+"F0.wireOp",EDGE,"E8"),sQuery(id+"F0.wireOp",EDGE,"E9"),sQuery(id+"F0.wireOp",EDGE,"E11"),sQuery(id+"F0.wireOp",EDGE,"E14"),subQ0])],"isStart":true})});}
            var sketch = newSketch(context, id + "F15", { "sketchPlane" : qUnion([Q0])});
            skLineSegment(sketch, "E95.bottom", {"start": v(44.5, -78) * mm, "end": v(0, -78) * mm});
            skLineSegment(sketch, "E95.top", {"start": v(44.5, -87) * mm, "end": v(0, -87) * mm});
            skLineSegment(sketch, "E95.left", {"start": v(44.5, -78) * mm, "end": v(44.5, -87) * mm});
            skLineSegment(sketch, "E95.right", {"start": v(0, -78) * mm, "end": v(0, -87) * mm});
            skPoint(sketch, "E95.middle", {"position": v(22.25, -82.5) * mm});
            skSolve(sketch);
        }
        {
            var Q0;
            Q0 = qSketchRegion(id + "F15", true);
            extrude(context, id + "F16", {"entities" : qUnion([Q0]), "operationType" : NewBodyOperationType.ADD, "depth" : 1.5 * mm, "offsetDistance" : 25 * mm});
        }
        {
            var Q0;
            Q0=makeQuery(id+"F16.opExtrude","CAP_FACE",FACE,{"disambiguationData":[OSD([sQuery(id+"F15.wireOp",EDGE,"E95.bottom"),sQuery(id+"F15.wireOp",EDGE,"E95.top"),sQuery(id+"F15.wireOp",EDGE,"E95.left"),sQuery(id+"F15.wireOp",EDGE,"E95.right")])],"isStart":false});
            chamfer(context, id + "F17", {"entities" : qUnion([Q0]), "width" : 1.5 * mm, "tangentPropagation" : true});
        }
        {
            var Q0;
            Q0=makeQuery(id+"F16.opExtrude","CAP_FACE",FACE,{"disambiguationData":[OSD([sQuery(id+"F15.wireOp",EDGE,"E95.bottom"),sQuery(id+"F15.wireOp",EDGE,"E95.top"),sQuery(id+"F15.wireOp",EDGE,"E95.left"),sQuery(id+"F15.wireOp",EDGE,"E95.right")])],"isStart":true});
            extrude(context, id + "F18", {"entities" : qUnion([Q0]), "operationType" : NewBodyOperationType.REMOVE, "endBound" : BoundingType.THROUGH_ALL, "oppositeDirection" : true, "depth" : 25 * mm, "offsetDistance" : 25 * mm});
        }
        {
            var Q0;
            Q0=makeQuery(id+"F5.boolean.opBoolean","MERGE",EDGE,{"derivedFrom":[makeQuery(id+"F1.opExtrude","SWEPT_EDGE",EDGE,{"disambiguationData":[OSD([sQuery(id+"F0.wireOp",EDGE,"E0.top"),sQuery(id+"F0.wireOp",EDGE,"E0.right")])]}),makeQuery(id+"F5.opExtrude","SWEPT_EDGE",EDGE,{"disambiguationData":[OSD([sQuery(id+"F4.wireOp",EDGE,"E23.bottom"),sQuery(id+"F4.wireOp",EDGE,"E23.left")])]})]});
            var Q1;
            Q1=makeQuery(id+"F5.boolean.opBoolean","MERGE",EDGE,{"derivedFrom":[makeQuery(id+"F1.opExtrude","SWEPT_EDGE",EDGE,{"disambiguationData":[OSD([sQuery(id+"F0.wireOp",EDGE,"E0.top"),sQuery(id+"F0.wireOp",EDGE,"E0.left")])]}),makeQuery(id+"F5.opExtrude","SWEPT_EDGE",EDGE,{"disambiguationData":[OSD([sQuery(id+"F4.wireOp",EDGE,"E22.bottom"),sQuery(id+"F4.wireOp",EDGE,"E22.left")])]})]});
            var Q2;
            Q2=makeQuery(id+"F5.boolean.opBoolean","MERGE",EDGE,{"derivedFrom":[makeQuery(id+"F1.opExtrude","SWEPT_EDGE",EDGE,{"disambiguationData":[OSD([sQuery(id+"F0.wireOp",EDGE,"E0.bottom"),sQuery(id+"F0.wireOp",EDGE,"E0.left")])]}),makeQuery(id+"F5.opExtrude","SWEPT_EDGE",EDGE,{"disambiguationData":[OSD([sQuery(id+"F4.wireOp",EDGE,"E19.bottom"),sQuery(id+"F4.wireOp",EDGE,"E19.left")])]})]});
            var Q3;
            Q3=makeQuery(id+"F5.boolean.opBoolean","MERGE",EDGE,{"derivedFrom":[makeQuery(id+"F1.opExtrude","SWEPT_EDGE",EDGE,{"disambiguationData":[OSD([sQuery(id+"F0.wireOp",EDGE,"E0.bottom"),sQuery(id+"F0.wireOp",EDGE,"E0.right")])]}),makeQuery(id+"F5.opExtrude","SWEPT_EDGE",EDGE,{"disambiguationData":[OSD([sQuery(id+"F4.wireOp",EDGE,"E20.bottom"),sQuery(id+"F4.wireOp",EDGE,"E20.left")])]})]});
            chamfer(context, id + "F19", {"entities" : qUnion([Q0, Q1, Q2, Q3]), "width" : 2 * mm, "tangentPropagation" : true});
        }
    });
